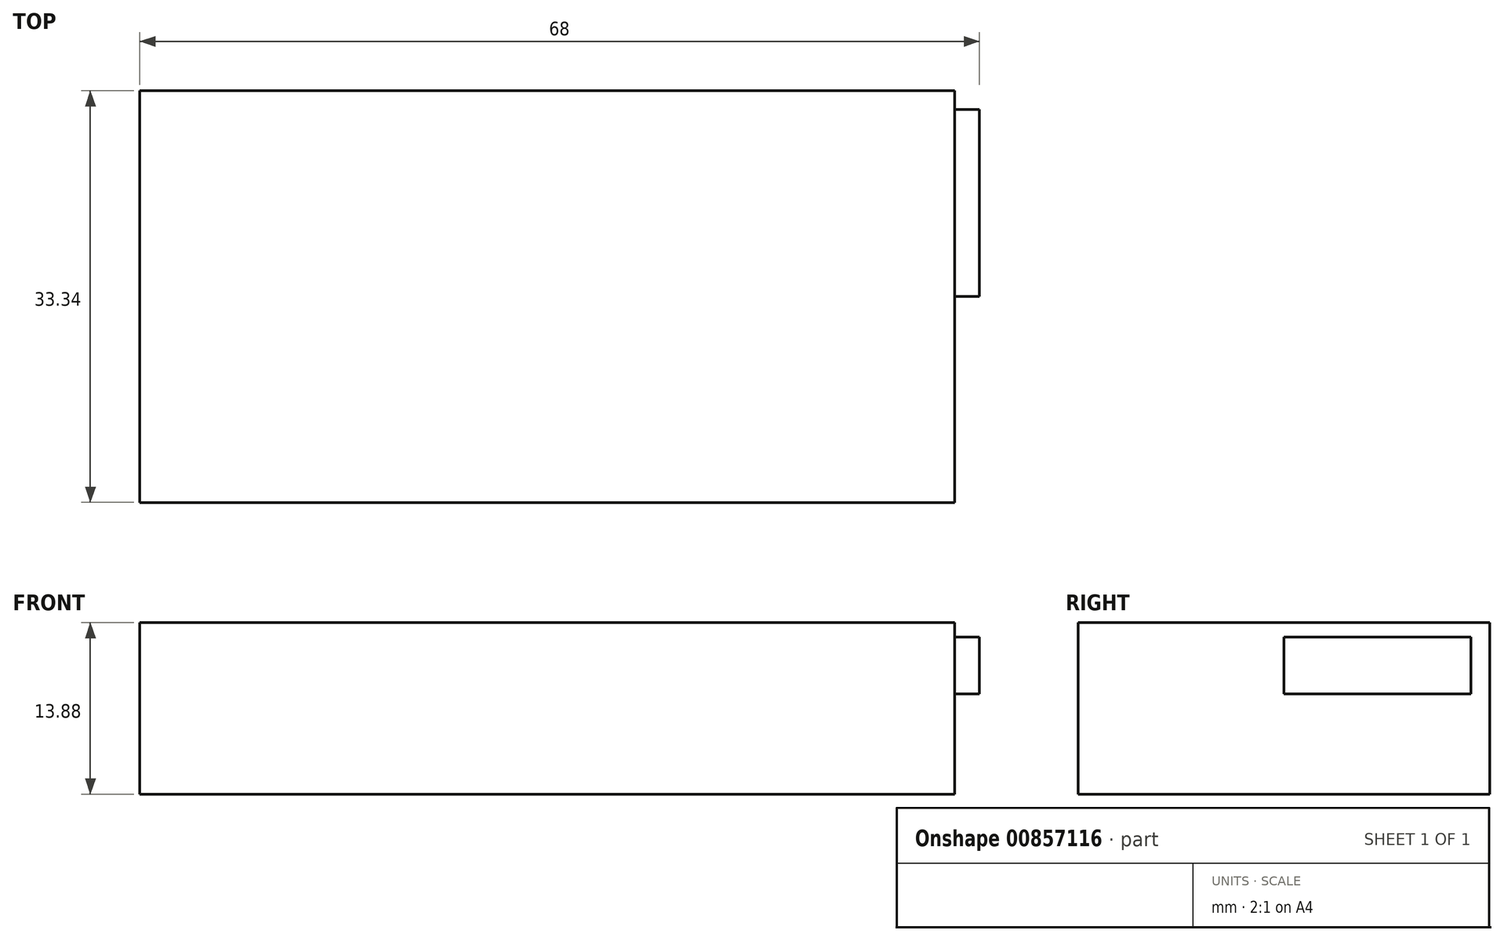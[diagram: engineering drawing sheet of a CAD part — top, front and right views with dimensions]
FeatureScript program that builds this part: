
annotation { "Feature Type Name" : "Feature", "Feature Type Description" : "" }
export const myFeature = defineFeature(function(context is Context, id is Id, definition is map)
    precondition{}
    {
        {
            var Q0;
            Q0=qCreatedBy(makeId("Top.planeOp"),FACE);
            var sketch = newSketch(context, id + "F0", { "sketchPlane" : qUnion([Q0])});
            skLineSegment(sketch, "E0.bottom", {"start": v(33, 16.68) * mm, "end": v(-33, 16.68) * mm});
            skLineSegment(sketch, "E0.top", {"start": v(33, -16.68) * mm, "end": v(-33, -16.68) * mm});
            skLineSegment(sketch, "E0.left", {"start": v(33, 16.68) * mm, "end": v(33, -16.68) * mm});
            skLineSegment(sketch, "E0.right", {"start": v(-33, 16.68) * mm, "end": v(-33, -16.68) * mm});
            skPoint(sketch, "E0.middle", {"position": v(0, 0) * mm});
            skSolve(sketch);
        }
        {
            var Q0;
            Q0=makeQuery(id+"F0.imprint","IMPRINT",FACE,{"disambiguationData":[TD([[makeQuery(id+"F0.imprint","IMPRINT",EDGE,{"derivedFrom":sQuery(id+"F0.wireOp",EDGE,"E0.bottom")}),1.0]])]});
            extrude(context, id + "F1", {"entities" : qUnion([Q0]), "depth" : 13.88 * mm, "offsetDistance" : 25.4 * mm});
        }
        {
            var Q0;
            Q0=makeQuery(id+"F1.opExtrude","SWEPT_FACE",FACE,{"disambiguationData":[OSD([sQuery(id+"F0.wireOp",EDGE,"E0.left")])]});
            var sketch = newSketch(context, id + "F2", { "sketchPlane" : qUnion([Q0])});
            skLineSegment(sketch, "E1.bottom", {"start": v(0, 12.73) * mm, "end": v(15.15, 12.73) * mm});
            skLineSegment(sketch, "E1.top", {"start": v(0, 8.1) * mm, "end": v(15.15, 8.1) * mm});
            skLineSegment(sketch, "E1.left", {"start": v(0, 12.73) * mm, "end": v(0, 8.1) * mm});
            skLineSegment(sketch, "E1.right", {"start": v(15.15, 12.73) * mm, "end": v(15.15, 8.1) * mm});
            skSolve(sketch);
        }
        {
            var Q0;
            Q0=makeQuery(id+"F2.imprint","IMPRINT",FACE,{"disambiguationData":[TD([[makeQuery(id+"F2.imprint","IMPRINT",EDGE,{"derivedFrom":sQuery(id+"F2.wireOp",EDGE,"E1.bottom")}),-1.0]])]});
            extrude(context, id + "F3", {"entities" : qUnion([Q0]), "operationType" : NewBodyOperationType.ADD, "depth" : 2 * mm, "offsetDistance" : 25 * mm});
        }
    });
